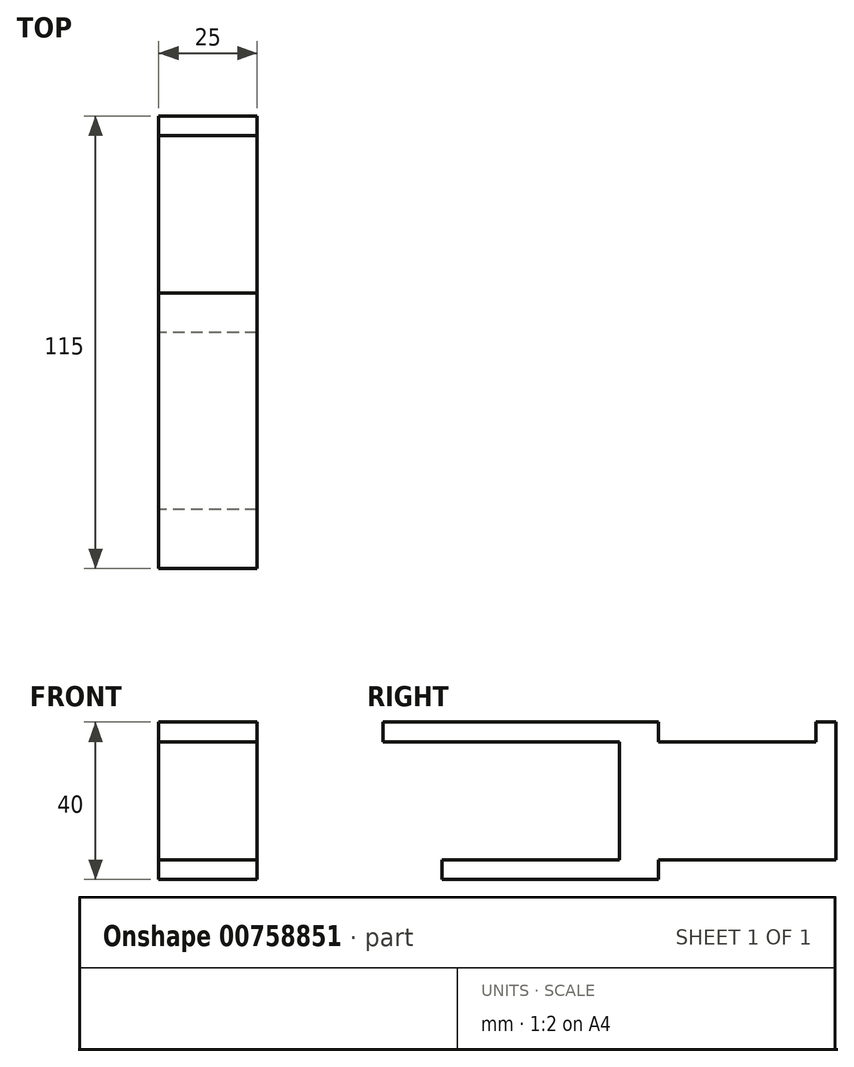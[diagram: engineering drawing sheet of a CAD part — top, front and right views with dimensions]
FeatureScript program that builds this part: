
annotation { "Feature Type Name" : "Feature", "Feature Type Description" : "" }
export const myFeature = defineFeature(function(context is Context, id is Id, definition is map)
    precondition{}
    {
        {
            var Q0;
            Q0=qCreatedBy(makeId("Right.planeOp"),FACE);
            var sketch = newSketch(context, id + "F0", { "sketchPlane" : qUnion([Q0])});
            skLineSegment(sketch, "E0.left", {"start": v(0, 0) * mm, "end": v(0, -30) * mm});
            skLineSegment(sketch, "E1.bottom", {"start": v(0, 0) * mm, "end": v(-60, 0) * mm});
            skLineSegment(sketch, "E1.top", {"start": v(10, 5) * mm, "end": v(-60, 5) * mm});
            skLineSegment(sketch, "E1.right", {"start": v(-60, 0) * mm, "end": v(-60, 5) * mm});
            skLineSegment(sketch, "E2", {"start": v(0, -30) * mm, "end": v(-45, -30) * mm});
            skLineSegment(sketch, "E3", {"start": v(0, -30) * mm, "end": v(10, -30) * mm, "construction": true});
            skLineSegment(sketch, "E4.bottom", {"start": v(10, 0) * mm, "end": v(50, 0) * mm});
            skLineSegment(sketch, "E4.top", {"start": v(10, -30) * mm, "end": v(53, -30) * mm});
            skLineSegment(sketch, "E5.bottom", {"start": v(50, 5) * mm, "end": v(55, 5) * mm});
            skLineSegment(sketch, "E6.trimOffspring", {"start": v(10, -30) * mm, "end": v(10, -35) * mm});
            skLineSegment(sketch, "E7", {"start": v(10, 5) * mm, "end": v(10, 0) * mm});
            skLineSegment(sketch, "E8", {"start": v(50, 5) * mm, "end": v(50, 0) * mm});
            skLineSegment(sketch, "E9", {"start": v(0, 0) * mm, "end": v(10, 0) * mm, "construction": true});
            skLineSegment(sketch, "E10", {"start": v(53, -30) * mm, "end": v(55, -30) * mm});
            skLineSegment(sketch, "E11", {"start": v(55, 5) * mm, "end": v(55, -30) * mm});
            skLineSegment(sketch, "E12", {"start": v(10, -35) * mm, "end": v(-45, -35) * mm});
            skLineSegment(sketch, "E13", {"start": v(-45, -35) * mm, "end": v(-45, -30) * mm});
            skSolve(sketch);
        }
        {
            var Q0;
            Q0=makeQuery(id+"F0.imprint","IMPRINT",FACE,{"disambiguationData":[TD([[makeQuery(id+"F0.imprint","IMPRINT",EDGE,{"derivedFrom":sQuery(id+"F0.wireOp",EDGE,"E0.left")}),1.0]])]});
            extrude(context, id + "F1", {"entities" : qUnion([Q0]), "depth" : 25 * mm, "offsetDistance" : 25 * mm});
        }
    });
